# Revit family: IS_UltraFlatS_K8214_BIM_DE
name_source: partatom
category: Plumbing Fixtures
revit_build: Autodesk Revit MEP 2015 (Build: 20140606_1530(x64)
units: mm (PartAtom-declared; Revit-internal decimal feet)

## types (5) — shared parameters
Assembly Code = C1030200
Description = ULTRA FLAT S square shower tray 800x800mm
DrainSize = 90 mm
HasTray = No
IfcExportAs = IfcSanitaryTerminalType
IfcExportType = SHOWER
ManufacturerURL = www.idealstandard.com
Material = Composite Material
Name = ULTRA FLAT S square shower tray 800x800mm
NettWeight = 22,7 kg
NominalHeight = 30 mm  [stored 0.0984252 ft]
NominalLength = 800 mm
NominalWidth = 800 mm
ProductInformation = www.idealstandard.de/produkte
Shape = Rectangular
Size = 800x800x30
Space = Internal
SpareParts = www.idealstandard.de/ersatzteile
URL = www.idealstandard.com
Version = 1
VolumeUnits = Litres
WarrantyDurationUnit = year
zero-valued in all types: CWFU, Cost, Default Elevation, HWFU, NominalDepth, WFU

## per-type parameters (varying)
| type | Model | ModelNumber |
| K8214FR - ULTRA FLAT S square shower tray 800x800mm | K8214FR | K8214FR |
| K8214FS - ULTRA FLAT S square shower tray 800x800mm | K8214FS | K8214FS |
| K8214FT -ULTRA FLAT S square shower tray 800x800mm | K8214FT | K8214FT |
| K8214FV - ULTRA FLAT S square shower tray 800x800mm | K8214FV | K8214FV |
| K8214FU - ULTRA FLAT S square shower tray 800x800mm | K8214FU | K8214FU |

note: [stored X ft] marks values corroborated as IEEE doubles in the binary element streams (Revit-internal decimal feet)

## geometry (parser evidence)
native form markers: Blend x4, Sweep x1
no freeform markers — native parametric forms only
